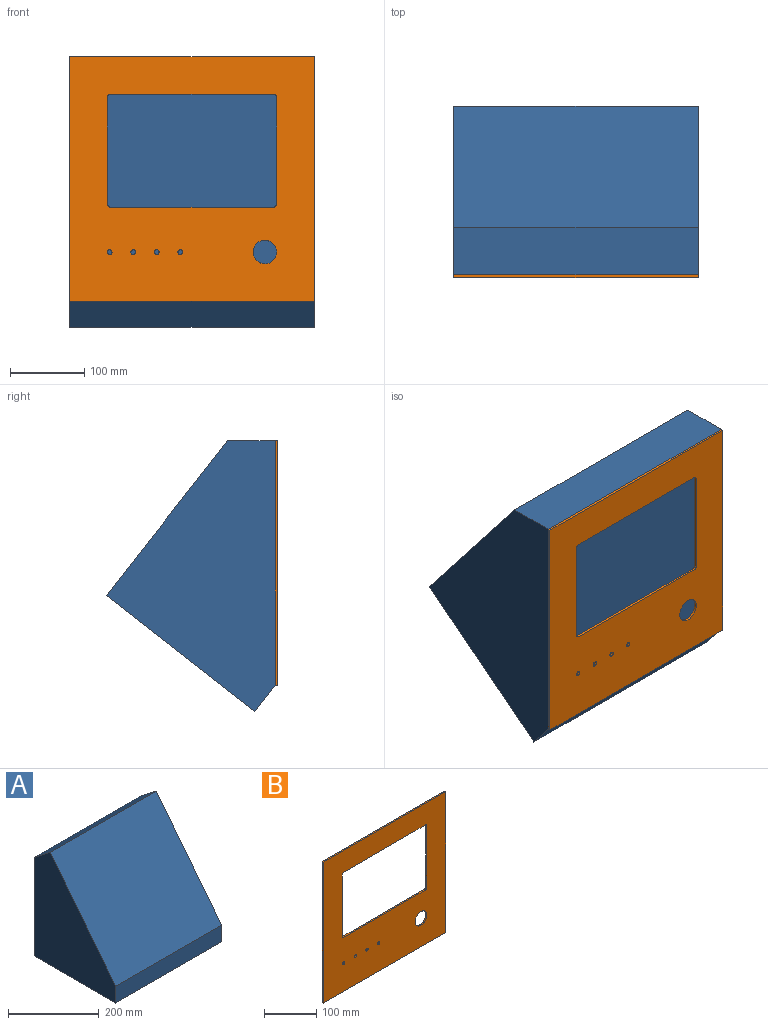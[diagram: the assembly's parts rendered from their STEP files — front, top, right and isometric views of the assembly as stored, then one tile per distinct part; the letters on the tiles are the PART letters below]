
ASSEMBLY  parts=2 mates=1
PART A: 7 faces, bbox 330.2x254x304.8 mm
  f0: plane 330.2x50.42mm, normal (0,0.62,0.79), area 21146.9mm2, adj f1,f4,f5,f6
  f1: plane 330.2x259.98mm, normal (0,-0.79,0.62), area 109032mm2, adj f0,f2,f5,f6
  f2: plane 330.2x44.82mm, normal (0,-1,0), area 14800.3mm2, adj f1,f3,f5,f6
  f3: plane 330.2x254mm, normal (0,0,-1), area 83870.8mm2, adj f2,f4,f5,f6
  f4: plane 330.2x265.32mm, normal (0,1,0), area 87607.3mm2, adj f0,f3,f5,f6
  f5: plane 304.8x254mm, normal (1,0,0), area 49961mm2, adj f0,f1,f2,f3,f4
  f6: plane 304.8x254mm, normal (-1,0,0), area 49961mm2, adj f0,f1,f2,f3,f4
PART B: 19 faces, bbox 330.2x3.2x330.2 mm
  f0: plane 330.2x330.2mm, normal (0,-1,0), area 73294.5mm2, adj f2,f3,f4,f5,f6,f7,f8,f9
  f1: plane 330.2x330.2mm, normal (0,1,0), area 73294.5mm2, adj f2,f3,f4,f5,f6,f7,f8,f9
  f2: plane 330.2x3.18mm, normal (0,0,1), area 1048.4mm2, adj f0,f1,f3,f5
  f3: plane 330.2x3.18mm, normal (-1,0,0), area 1048.4mm2, adj f0,f1,f2,f4
  f4: plane 330.2x3.18mm, normal (0,0,-1), area 1048.4mm2, adj f0,f1,f3,f5
  f5: plane 330.2x3.18mm, normal (1,0,0), area 1048.4mm2, adj f0,f1,f2,f4
  f6: plane 219.08x3.18mm, normal (0,0,-1), area 695.6mm2, adj f0,f1,f7,f13
  f7: cylinder r=4.76mm len=4.76mm, axis (0,1,0), area 23.8mm2, adj f0,f1,f6,f8
  f8: plane 142.88x3.18mm, normal (1,0,0), area 453.6mm2, adj f0,f1,f7,f9
  f9: cylinder r=4.76mm len=4.76mm, axis (0,1,0), area 23.8mm2, adj f0,f1,f8,f10
  f10: plane 219.08x3.18mm, normal (0,0,1), area 695.6mm2, adj f0,f1,f9,f11
  f11: cylinder r=4.76mm len=4.76mm, axis (0,1,0), area 23.8mm2, adj f0,f1,f10,f12
  f12: plane 142.88x3.18mm, normal (-1,0,0), area 453.6mm2, adj f0,f1,f11,f13
  f13: cylinder r=4.76mm len=4.76mm, axis (0,1,0), area 23.8mm2, adj f0,f1,f6,f12
  f14: cylinder r=3.17mm len=6.35mm, axis (0,1,0), area 63.3mm2, adj f0,f1
  f15: cylinder r=3.17mm len=6.35mm, axis (0,1,0), area 63.3mm2, adj f0,f1
  f16: cylinder r=3.17mm len=6.35mm, axis (0,1,0), area 63.3mm2, adj f0,f1
  f17: cylinder r=3.17mm len=6.35mm, axis (0,1,0), area 63.3mm2, adj f0,f1
  f18: cylinder r=15.88mm len=31.75mm, axis (0,1,0), area 316.7mm2, adj f0,f1
PLACE A rot(axis=(1,0,0),38.1deg) t=(41.4,-157.88,70.1)mm
PLACE B t=(206.5,-191.55,72.21)mm
MATE planar A.f1 <-> B.f1  axis (0,-1,0) through (206.5,-191.55,72.21)mm
